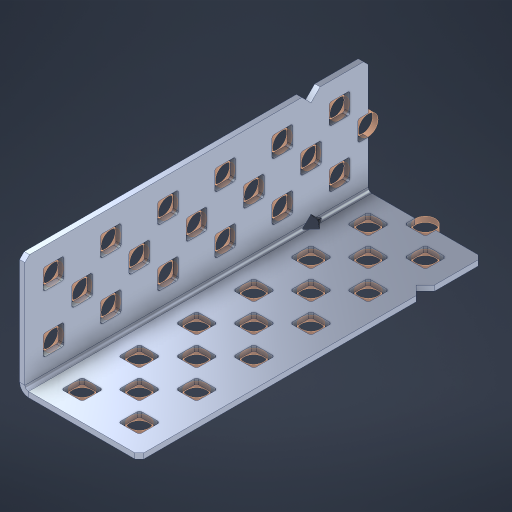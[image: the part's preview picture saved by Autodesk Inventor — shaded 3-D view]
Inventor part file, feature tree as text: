
AUTODESK INVENTOR PART (.ipt)
format: ipt  version: 2023 (Build 270158000, 158)  size: 749,568 bytes
history: native  units: in
note: dims shown in document units (in); Inventor stores cm internally (conversion verified against a paired STEP export)
features: other x42, extrude x34, sheet_metal_op x8, sketch x7, pattern_linear x2, mirror x1, chamfer x1
ambient origin geometry x8: Origin, YZ Plane, XZ Plane, XY Plane, X Axis, Y Axis, Z Axis, Center Point
bodies: Solid1 (feature_tree), Body (feature_tree)
feature tree (95):
  sheet_metal_op  "Flanges"
  sheet_metal_op  "Body Pattern"
  pattern_linear  "Center Pattern"  Spacing1=1.0in  [1 undecoded]
  other  "Arc Length"
  pattern_linear  "Notch Pattern"  Spacing1=0.1875in  [1 undecoded]
  other  "Diagonal Plane"
  mirror  "Everything Mirrored"
  chamfer  "End Chamfer"
  sketch  "Sketch1"  dims[d0=1.0in]
  other  "Plate1"
  sketch  "Sketch2"  dims[d1=3.0in]
  other  "Plate2"
  sheet_metal_op  "Bend1"
  sheet_metal_op  "Corner1"
  sketch  "Sketch8"  dims[d2=0.0469in]
  sketch  "Sketch9"  dims[d3=0.0469in]
  other  "Srf91"
  sheet_metal_op  "Body Pattern Sketch"
  other  "Srf92"
  sketch  "Sketch13"  dims[d4=0.0234in]
  sketch  "Sketch15"  dims[d5=0.0938in]
  sketch  "Sketch16"  dims[d6=0.0469in d7=1.0in d8=90.0deg d9=0.0312in d10=0.1875in d11=0.0469in d12=0.0469in d49=0.182in d50=0.02in d52=0.25in d53=0.0469in d54=0.0in d55=0.172in d56=1.0in d57=0.0in d60=2.3622in d62=0.5in d63=0.7874in d65=0.5in d85=0.1473in d86=0.1659in d89=0.0469in d90=0.0in d91=0.04in d92=0.0491in d95=2.5in d96=0.04in d97=0.25in d98=45.0deg d99=0.25in d106=0.182in d107=0.02in d108=0.5in d110=0.0469in d111=0.0in d112=0.172in d113=0.5in d114=0.0in d117=0.5in d123=0.25in d125=0.25in d126=0.0491in d127=0.1227in d128=0.08in d129=0.04in d130=2.5in]
  other  "Srf786"
  other  "Srf856"
  other  "Srf857"
  other  "Srf858"
  other  "Srf859"
  other  "Srf860"
  other  "Srf861"
  other  "Srf889"
  other  "Srf890"
  other  "Srf891"
  other  "Srf1275"
  other  "Srf1276"
  other  "Srf1278"
  other  "Srf1279"
  other  "Srf1280"
  other  "Srf1281"
  other  "Srf1282"
  other  "Srf1283"
  other  "Srf1277"
  other  "Srf1285"
  other  "Srf1286"
  other  "Srf1287"
  other  "Srf1383"
  other  "Srf1384"
  other  "Srf1385"
  other  "Srf1386"
  other  "Srf1445"
  other  "Srf1446"
  other  "Srf1475"
  other  "Srf1476"
  other  "Srf1477"
  other  "Srf1478"
  other  "Srf1537"
  other  "Srf1538"
  sheet_metal_op  "Body Stamp"
  sheet_metal_op  "Body Circle"
  other  "Center Stamp"
  other  "Center Circle"
  sheet_metal_op  "Notch"
  extrude  "ExtrusionSrf92"  Depth=0.0469in
  extrude  "ExtrusionSrf856"  Depth=0.0469in
  extrude  "ExtrusionSrf857"  Depth=0.182in
  extrude  "ExtrusionSrf858"  Depth=0.02in
  extrude  "ExtrusionSrf859"  Depth=0.25in
  extrude  "ExtrusionSrf860"  Depth=0.0469in
  extrude  "ExtrusionSrf861"  TaperAngle=0.0deg  [1 undecoded]
  extrude  "ExtrusionSrf889"  Depth=2.5in
  extrude  "ExtrusionSrf890"  Depth=1.0in TaperAngle=0.0deg
  extrude  "ExtrusionSrf891"  Depth=2.5in
  extrude  "ExtrusionSrf1275"  Depth=0.5in
  extrude  "ExtrusionSrf1276"  Depth=2.5in
  extrude  "ExtrusionSrf1277"  Depth=2.5in
  extrude  "ExtrusionSrf1278"  Depth=0.0469in
  extrude  "ExtrusionSrf1279"  Depth=2.5in TaperAngle=0.0deg
  extrude  "ExtrusionSrf1280"  Depth=2.5in
  extrude  "ExtrusionSrf1281"  Depth=0.25in TaperAngle=45.0deg
  extrude  "ExtrusionSrf1282"  Depth=0.25in
  extrude  "ExtrusionSrf1345"  Depth=0.182in
  extrude  "ExtrusionSrf1346"  Depth=0.02in
  extrude  "ExtrusionSrf1347"  Depth=0.5in
  extrude  "ExtrusionSrf1348"  Depth=0.0469in
  extrude  "ExtrusionSrf1383"  TaperAngle=0.0deg  [1 undecoded]
  extrude  "ExtrusionSrf1384"  Depth=2.5in
  extrude  "ExtrusionSrf1385"  Depth=0.5in TaperAngle=0.0deg
  extrude  "ExtrusionSrf1386"  Depth=0.5in
  extrude  "ExtrusionSrf1445"  Depth=0.25in
  extrude  "ExtrusionSrf1446"  Depth=0.25in
  extrude  "ExtrusionSrf1475"  Depth=2.5in
  extrude  "ExtrusionSrf1476"  Depth=2.5in
  extrude  "ExtrusionSrf1477"  Depth=2.5in
  extrude  "ExtrusionSrf1478"  Depth=2.5in
  extrude  "ExtrusionSrf1537"  Depth=2.5in
  extrude  "ExtrusionSrf1538"  [1 undecoded]
note: 5 required parameter values undecoded (feature->parameter linkage not recoverable at this tier; creation-order binding heuristic only, values carry confidence <= 0.55)
